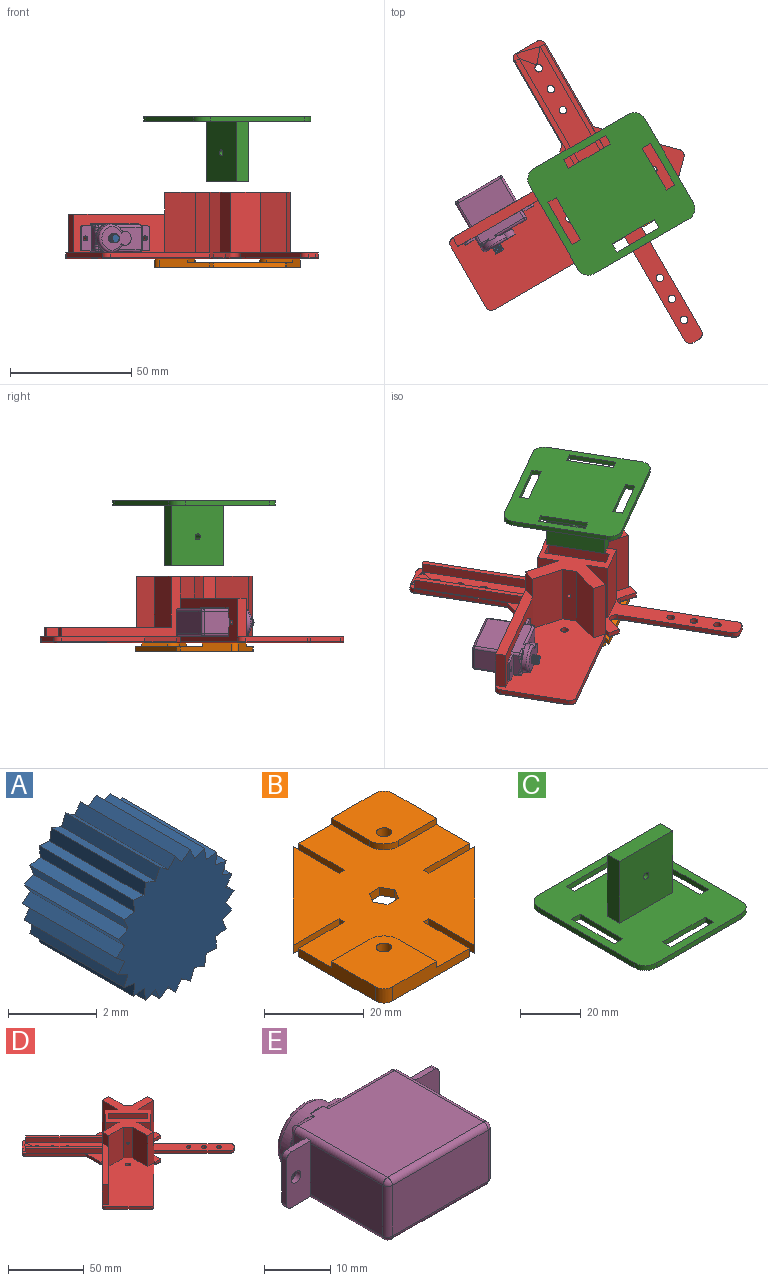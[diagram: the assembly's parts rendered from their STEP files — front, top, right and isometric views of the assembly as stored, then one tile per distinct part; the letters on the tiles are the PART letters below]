
ASSEMBLY  parts=5 mates=4
PART A: 50 faces, bbox 3.8x3x3.8 mm
  f0: plane 3x0.26mm, normal (0.78,0,-0.63), area 1mm2, adj f1,f47,f48,f49
  f1: plane 3x0.27mm, normal (-0.59,0,-0.81), area 1mm2, adj f0,f2,f48,f49
  f2: plane 3x0.31mm, normal (0.92,0,-0.4), area 1mm2, adj f1,f3,f48,f49
  f3: plane 3x0.32mm, normal (-0.36,0,-0.93), area 1mm2, adj f2,f4,f48,f49
  f4: plane 3x0.33mm, normal (0.99,0,-0.15), area 1mm2, adj f3,f5,f48,f49
  f5: plane 3x0.34mm, normal (-0.11,0,-0.99), area 1mm2, adj f4,f6,f48,f49
  f6: plane 3x0.34mm, normal (0.99,0,0.11), area 1mm2, adj f5,f7,f48,f49
  f7: plane 3x0.33mm, normal (0.15,0,-0.99), area 1mm2, adj f6,f8,f48,f49
  f8: plane 3x0.32mm, normal (0.93,0,0.36), area 1mm2, adj f7,f9,f48,f49
  f9: plane 3x0.31mm, normal (0.4,0,-0.92), area 1mm2, adj f8,f10,f48,f49
  f10: plane 3x0.27mm, normal (0.81,0,0.59), area 1mm2, adj f9,f11,f48,f49
  f11: plane 3x0.26mm, normal (0.63,0,-0.78), area 1mm2, adj f10,f12,f48,f49
  f12: plane 3x0.26mm, normal (0.63,0,0.78), area 1mm2, adj f11,f13,f48,f49
  f13: plane 3x0.27mm, normal (0.81,0,-0.59), area 1mm2, adj f12,f14,f48,f49
  f14: plane 3x0.31mm, normal (0.4,0,0.92), area 1mm2, adj f13,f15,f48,f49
  f15: plane 3x0.32mm, normal (0.93,0,-0.36), area 1mm2, adj f14,f16,f48,f49
  f16: plane 3x0.33mm, normal (0.15,0,0.99), area 1mm2, adj f15,f17,f48,f49
  f17: plane 3x0.34mm, normal (0.99,0,-0.11), area 1mm2, adj f16,f18,f48,f49
  f18: plane 3x0.34mm, normal (-0.11,0,0.99), area 1mm2, adj f17,f19,f48,f49
  f19: plane 3x0.33mm, normal (0.99,0,0.15), area 1mm2, adj f18,f20,f48,f49
  f20: plane 3x0.32mm, normal (-0.36,0,0.93), area 1mm2, adj f19,f21,f48,f49
  f21: plane 3x0.31mm, normal (0.92,0,0.4), area 1mm2, adj f20,f22,f48,f49
  f22: plane 3x0.27mm, normal (-0.59,0,0.81), area 1mm2, adj f21,f23,f48,f49
  f23: plane 3x0.26mm, normal (0.78,0,0.63), area 1mm2, adj f22,f24,f48,f49
  f24: plane 3x0.26mm, normal (-0.78,0,0.63), area 1mm2, adj f23,f25,f48,f49
  f25: plane 3x0.27mm, normal (0.59,0,0.81), area 1mm2, adj f24,f26,f48,f49
  f26: plane 3x0.31mm, normal (-0.92,0,0.4), area 1mm2, adj f25,f27,f48,f49
  f27: plane 3x0.32mm, normal (0.36,0,0.93), area 1mm2, adj f26,f28,f48,f49
  f28: plane 3x0.33mm, normal (-0.99,0,0.15), area 1mm2, adj f27,f29,f48,f49
  f29: plane 3x0.34mm, normal (0.11,0,0.99), area 1mm2, adj f28,f30,f48,f49
  f30: plane 3x0.34mm, normal (-0.99,0,-0.11), area 1mm2, adj f29,f31,f48,f49
  f31: plane 3x0.33mm, normal (-0.15,0,0.99), area 1mm2, adj f30,f32,f48,f49
  f32: plane 3x0.32mm, normal (-0.93,0,-0.36), area 1mm2, adj f31,f33,f48,f49
  f33: plane 3x0.31mm, normal (-0.4,0,0.92), area 1mm2, adj f32,f34,f48,f49
  f34: plane 3x0.27mm, normal (-0.81,0,-0.59), area 1mm2, adj f33,f35,f48,f49
  f35: plane 3x0.26mm, normal (-0.63,0,0.78), area 1mm2, adj f34,f36,f48,f49
  f36: plane 3x0.26mm, normal (-0.63,0,-0.78), area 1mm2, adj f35,f37,f48,f49
  f37: plane 3x0.27mm, normal (-0.81,0,0.59), area 1mm2, adj f36,f38,f48,f49
  f38: plane 3x0.31mm, normal (-0.4,0,-0.92), area 1mm2, adj f37,f39,f48,f49
  f39: plane 3x0.32mm, normal (-0.93,0,0.36), area 1mm2, adj f38,f40,f48,f49
  f40: plane 3x0.33mm, normal (-0.15,0,-0.99), area 1mm2, adj f39,f41,f48,f49
  f41: plane 3x0.34mm, normal (-0.99,0,0.11), area 1mm2, adj f40,f42,f48,f49
  f42: plane 3x0.34mm, normal (0.11,0,-0.99), area 1mm2, adj f41,f43,f48,f49
  f43: plane 3x0.33mm, normal (-0.99,0,-0.15), area 1mm2, adj f42,f44,f48,f49
  f44: plane 3x0.32mm, normal (0.36,0,-0.93), area 1mm2, adj f43,f45,f48,f49
  f45: plane 3x0.31mm, normal (-0.92,0,-0.4), area 1mm2, adj f44,f46,f48,f49
  f46: plane 3x0.27mm, normal (0.59,0,-0.81), area 1mm2, adj f45,f47,f48,f49
  f47: plane 3x0.26mm, normal (-0.78,0,-0.63), area 1mm2, adj f0,f46,f48,f49
  f48: plane 3.75x3.75mm, normal (0,-1,0), area 9.5mm2, adj f0,f1,f2,f3,f4,f5,f6,f7
  f49: plane 3.75x3.75mm, normal (0,1,0), area 9.5mm2, adj f0,f1,f2,f3,f4,f5,f6,f7
PART B: 38 faces, bbox 50x50x3.5 mm
  f0: plane 50x50mm, normal (0,0,1), area 1374.3mm2, adj f1,f2,f3,f4,f5,f6,f7,f8
  f1: plane 13x2mm, normal (-1,0,0), area 26mm2, adj f0,f2,f28,f29
  f2: plane 2x1.5mm, normal (0,1,0), area 3mm2, adj f0,f1,f3,f29
  f3: plane 13x2mm, normal (1,0,0), area 26mm2, adj f0,f2,f4,f29
  f4: plane 24.25x24.25mm, normal (-0.71,0.71,0), area 68.6mm2, adj f0,f3,f5,f29
  f5: plane 13x2mm, normal (0,-1,0), area 26mm2, adj f0,f4,f6,f29
  f6: plane 2x1.5mm, normal (-1,0,0), area 3mm2, adj f0,f5,f7,f29
  f7: plane 13x2mm, normal (0,1,0), area 26mm2, adj f0,f6,f8,f29
  f8: plane 21.75x3.5mm, normal (-1,0,0), area 62mm2, adj f0,f7,f9,f29,f34,f37
  f9: cylinder r=2.5mm len=3.5mm, axis (0,0,-1), area 13.7mm2, adj f8,f10,f29,f37
  f10: plane 21.75x3.5mm, normal (0,-1,0), area 62mm2, adj f0,f9,f11,f29,f35,f37
  f11: plane 13x2mm, normal (1,0,0), area 26mm2, adj f0,f10,f12,f29
  f12: plane 2x1.5mm, normal (0,-1,0), area 3mm2, adj f0,f11,f13,f29
  f13: plane 13x2mm, normal (-1,0,0), area 26mm2, adj f0,f12,f14,f29
  f14: plane 24.25x24.25mm, normal (0.71,-0.71,0), area 68.6mm2, adj f0,f13,f15,f29
  f15: plane 13x2mm, normal (0,1,0), area 26mm2, adj f0,f14,f16,f29
  f16: plane 2x1.5mm, normal (1,0,0), area 3mm2, adj f0,f15,f17,f29
  f17: plane 13x2mm, normal (0,-1,0), area 26mm2, adj f0,f16,f18,f29
  f18: plane 21.75x3.5mm, normal (1,0,0), area 62mm2, adj f0,f17,f19,f29,f32,f33
  f19: cylinder r=2.5mm len=3.5mm, axis (0,0,-1), area 13.7mm2, adj f18,f28,f29,f33
  f20: plane 2.68x2mm, normal (-0.87,0.5,0), area 6.2mm2, adj f0,f21,f25,f29
  f21: plane 3.1x2mm, normal (0,1,0), area 6.2mm2, adj f0,f20,f22,f29
  f22: plane 2.68x2mm, normal (0.87,0.5,0), area 6.2mm2, adj f0,f21,f23,f29
  f23: plane 2.68x2mm, normal (0.87,-0.5,0), area 6.2mm2, adj f0,f22,f24,f29
  f24: plane 3.1x2mm, normal (0,-1,0), area 6.2mm2, adj f0,f23,f25,f29
  f25: plane 2.68x2mm, normal (-0.87,-0.5,0), area 6.2mm2, adj f0,f20,f24,f29
  f26: cylinder r=1.55mm len=3.5mm, axis (0,0,-1), area 34.1mm2, adj f29,f33
  f27: cylinder r=1.55mm len=3.5mm, axis (0,0,-1), area 34.1mm2, adj f29,f37
  f28: plane 21.75x3.5mm, normal (0,1,0), area 62mm2, adj f0,f1,f19,f29,f30,f33
  f29: plane 50x50mm, normal (0,0,-1), area 1791.2mm2, adj f1,f2,f3,f4,f5,f6,f7,f8
  f30: plane 10.86x1.5mm, normal (-1,0,0), area 16.3mm2, adj f0,f28,f31,f33
  f31: cylinder r=4mm len=4mm, axis (0,0,-1), area 9.4mm2, adj f0,f30,f32,f33
  f32: plane 10.86x1.5mm, normal (0,-1,0), area 16.3mm2, adj f0,f18,f31,f33
  f33: plane 14.86x14.86mm, normal (0,0,1), area 208.4mm2, adj f18,f19,f26,f28,f30,f31,f32
  f34: plane 10.86x1.5mm, normal (0,1,0), area 16.3mm2, adj f0,f8,f36,f37
  f35: plane 10.86x1.5mm, normal (1,0,0), area 16.3mm2, adj f0,f10,f36,f37
  f36: cylinder r=4mm len=4mm, axis (0,0,-1), area 9.4mm2, adj f0,f34,f35,f37
  f37: plane 14.86x14.86mm, normal (0,0,1), area 208.4mm2, adj f8,f9,f10,f27,f34,f35,f36
PART C: 32 faces, bbox 50x55x27 mm
  f0: plane 55x50mm, normal (0,0,1), area 2263.5mm2, adj f1,f2,f3,f4,f5,f6,f7,f8
  f1: plane 4x2mm, normal (1,0,0), area 8mm2, adj f0,f2,f24,f25
  f2: plane 20x2mm, normal (0,-1,0), area 40mm2, adj f0,f1,f3,f25
  f3: plane 4x2mm, normal (-1,0,0), area 8mm2, adj f0,f2,f24,f25
  f4: plane 45x2mm, normal (1,0,0), area 90mm2, adj f0,f5,f20,f25
  f5: cylinder r=5mm len=5mm, axis (0,0,-1), area 15.7mm2, adj f0,f4,f6,f25
  f6: plane 40x2mm, normal (0,1,0), area 80mm2, adj f0,f5,f7,f25
  f7: cylinder r=5mm len=5mm, axis (0,0,-1), area 15.7mm2, adj f0,f6,f8,f25
  f8: plane 45x2mm, normal (-1,0,0), area 90mm2, adj f0,f7,f9,f25
  f9: cylinder r=5mm len=5mm, axis (0,0,-1), area 15.7mm2, adj f0,f8,f10,f25
  f10: plane 40x2mm, normal (0,-1,0), area 80mm2, adj f0,f9,f20,f25
  f11: plane 4x2mm, normal (0,-1,0), area 8mm2, adj f0,f12,f21,f25
  f12: plane 20x2mm, normal (-1,0,0), area 40mm2, adj f0,f11,f13,f25
  f13: plane 4x2mm, normal (0,1,0), area 8mm2, adj f0,f12,f21,f25
  f14: plane 20x2mm, normal (1,0,0), area 40mm2, adj f0,f15,f22,f25
  f15: plane 4x2mm, normal (0,-1,0), area 8mm2, adj f0,f14,f16,f25
  f16: plane 20x2mm, normal (-1,0,0), area 40mm2, adj f0,f15,f22,f25
  f17: plane 4x2mm, normal (1,0,0), area 8mm2, adj f0,f18,f23,f25
  f18: plane 20x2mm, normal (0,-1,0), area 40mm2, adj f0,f17,f19,f25
  f19: plane 4x2mm, normal (-1,0,0), area 8mm2, adj f0,f18,f23,f25
  f20: cylinder r=5mm len=5mm, axis (0,0,-1), area 15.7mm2, adj f0,f4,f10,f25
  f21: plane 20x2mm, normal (1,0,0), area 40mm2, adj f0,f11,f13,f25
  f22: plane 4x2mm, normal (0,1,0), area 8mm2, adj f0,f14,f16,f25
  f23: plane 20x2mm, normal (0,1,0), area 40mm2, adj f0,f17,f19,f25
  f24: plane 20x2mm, normal (0,1,0), area 40mm2, adj f0,f1,f3,f25
  f25: plane 55x50mm, normal (0,0,-1), area 2408.5mm2, adj f1,f2,f3,f4,f5,f6,f7,f8
  f26: plane 25x25mm, normal (0,1,0), area 620.1mm2, adj f0,f27,f29,f30,f31
  f27: plane 25x5.8mm, normal (-1,0,0), area 145mm2, adj f0,f26,f28,f30
  f28: plane 25x25mm, normal (0,-1,0), area 620.1mm2, adj f0,f27,f29,f30,f31
  f29: plane 25x5.8mm, normal (1,0,0), area 145mm2, adj f0,f26,f28,f30
  f30: plane 25x5.8mm, normal (0,0,1), area 145mm2, adj f26,f27,f28,f29
  f31: cylinder r=1.25mm len=5.8mm, axis (0,-1,0), area 45.6mm2, adj f26,f28
PART D: 144 faces, bbox 111x113.5x27.5 mm
  f0: plane 25x9.9mm, normal (-0.71,0.71,0), area 334mm2, adj f1,f66,f67,f75,f138,f140,f142,f143
  f1: plane 53.02x53.02mm, normal (0,0,1), area 782.5mm2, adj f0,f11,f12,f13,f14,f15,f16,f17
  f2: plane 58.57x52.57mm, normal (0,0,1), area 1637.9mm2, adj f22,f23,f24,f25,f26,f48,f68,f69
  f3: plane 9x6mm, normal (-1,0,0), area 54mm2, adj f21,f68,f75,f86
  f4: plane 50.54x50.54mm, normal (0,0,1), area 540.4mm2, adj f29,f30,f31,f32,f33,f34,f35,f36
  f5: plane 18.25x18.25mm, normal (0,0,1), area 315.2mm2, adj f6,f7,f8,f49,f63,f64,f65
  f6: plane 27x21.75mm, normal (1,0,0), area 193.5mm2, adj f5,f7,f52,f63,f75,f133
  f7: cylinder r=2.5mm len=2.5mm, axis (0,0,-1), area 7.9mm2, adj f5,f6,f8,f131
  f8: plane 27x21.75mm, normal (0,1,0), area 193.5mm2, adj f5,f7,f9,f65,f75,f129
  f9: plane 27x17.5mm, normal (-1,0,0), area 431.3mm2, adj f8,f10,f55,f66,f75,f127
  f10: plane 2x1.5mm, normal (0,1,0), area 3mm2, adj f9,f11,f55,f125
  f11: plane 17.5x2mm, normal (1,0,0), area 35mm2, adj f1,f10,f12,f55,f123
  f12: plane 13.64x2mm, normal (0,1,0), area 27.3mm2, adj f1,f11,f13,f121
  f13: plane 28.03x28.03mm, normal (0.71,0.71,0), area 79.3mm2, adj f1,f12,f14,f119
  f14: cylinder r=2.5mm len=3.54mm, axis (0,0,-1), area 7.9mm2, adj f1,f13,f15,f117
  f15: plane 7.07x7.07mm, normal (-0.71,0.71,0), area 20mm2, adj f1,f14,f16,f115
  f16: cylinder r=2.5mm len=3.54mm, axis (0,0,-1), area 7.9mm2, adj f1,f15,f17,f113
  f17: plane 28.03x28.03mm, normal (-0.71,-0.71,0), area 79.3mm2, adj f1,f16,f18,f111
  f18: plane 13.64x2mm, normal (-1,0,0), area 27.3mm2, adj f1,f17,f19,f109
  f19: plane 17.5x2mm, normal (0,-1,0), area 35mm2, adj f1,f18,f20,f56,f107
  f20: plane 2x1.5mm, normal (-1,0,0), area 3mm2, adj f19,f21,f56,f105
  f21: plane 27x17.5mm, normal (0,1,0), area 431.3mm2, adj f3,f20,f22,f56,f67,f75,f103
  f22: plane 33.59x33.59mm, normal (-0.71,0.71,0), area 573.5mm2, adj f2,f21,f23,f77,f78,f79,f80,f81
  f23: cylinder r=2.5mm len=3.54mm, axis (0,0,-1), area 7.9mm2, adj f2,f22,f24,f99
  f24: plane 20.71x20.71mm, normal (-0.71,-0.71,0), area 58.6mm2, adj f2,f23,f25,f100
  f25: cylinder r=2.5mm len=3.54mm, axis (0,0,-1), area 7.9mm2, adj f2,f24,f26,f102
  f26: plane 33.59x33.59mm, normal (0.71,-0.71,0), area 95mm2, adj f2,f25,f27,f104
  f27: plane 27x17.5mm, normal (1,0,0), area 431.3mm2, adj f26,f28,f57,f71,f72,f75,f106
  f28: plane 2x1.5mm, normal (0,-1,0), area 3mm2, adj f27,f29,f57,f108
  f29: plane 17.5x2mm, normal (-1,0,0), area 35mm2, adj f4,f28,f30,f57,f110
  f30: plane 5x2mm, normal (0,-1,0), area 10mm2, adj f4,f29,f31,f112
  f31: plane 7.56x2mm, normal (1,0,0), area 15.1mm2, adj f4,f30,f32,f114
  f32: cylinder r=2.5mm len=4.27mm, axis (0,0,-1), area 11.8mm2, adj f4,f31,f33,f116
  f33: plane 34.88x34.88mm, normal (-0.71,-0.71,0), area 98.7mm2, adj f4,f32,f34,f118
  f34: cylinder r=2.5mm len=3.54mm, axis (0,0,-1), area 7.9mm2, adj f4,f33,f35,f120
  f35: plane 2.12x2.12mm, normal (0.71,-0.71,0), area 6mm2, adj f4,f34,f36,f122
  f36: cylinder r=2.5mm len=3.54mm, axis (0,0,-1), area 7.9mm2, adj f4,f35,f37,f124
  f37: plane 34.88x34.88mm, normal (0.71,0.71,0), area 98.7mm2, adj f4,f36,f38,f126
  f38: cylinder r=2.5mm len=4.27mm, axis (0,0,-1), area 11.8mm2, adj f4,f37,f39,f128
  f39: plane 7.56x2mm, normal (0,-1,0), area 15.1mm2, adj f4,f38,f40,f130
  f40: plane 5x2mm, normal (1,0,0), area 10mm2, adj f4,f39,f41,f132
  f41: plane 17.5x2mm, normal (0,1,0), area 35mm2, adj f4,f40,f42,f58,f134
  f42: plane 2x1.5mm, normal (1,0,0), area 3mm2, adj f41,f52,f58,f136
  f43: cylinder r=1.55mm len=3.1mm, axis (0,0,-1), area 5.8mm2, adj f98,f137
  f44: cylinder r=1.55mm len=3.1mm, axis (0,0,-1), area 19.5mm2, adj f1,f97
  f45: cylinder r=1.55mm len=3.1mm, axis (0,0,-1), area 19.5mm2, adj f1,f96
  f46: cylinder r=1.55mm len=3.1mm, axis (0,0,-1), area 19.5mm2, adj f1,f95
  f47: cylinder r=1.55mm len=3.1mm, axis (0,0,-1), area 19.5mm2, adj f4,f94
  f48: cylinder r=1.55mm len=3.1mm, axis (0,0,-1), area 19.5mm2, adj f2,f93
  f49: cylinder r=1.55mm len=3.1mm, axis (0,0,-1), area 19.5mm2, adj f5,f92
  f50: cylinder r=1.55mm len=3.1mm, axis (0,0,-1), area 19.5mm2, adj f4,f91
  f51: cylinder r=1.55mm len=3.1mm, axis (0,0,-1), area 19.5mm2, adj f4,f90
  f52: plane 27x17.5mm, normal (0,-1,0), area 431.3mm2, adj f6,f42,f58,f62,f75,f135
  f53: plane 22.63x22.63mm, normal (0,0,1), area 128.7mm2, adj f59,f60,f61,f74,f137
  f54: plane 112.09x109.61mm, normal (0,0,-1), area 4089.8mm2, adj f90,f91,f92,f93,f94,f95,f96,f97
  f55: plane 3.15x1.5mm, normal (0,0,-1), area 3.6mm2, adj f9,f10,f11,f66
  f56: plane 3.15x1.5mm, normal (0,0,-1), area 3.6mm2, adj f19,f20,f21,f67
  f57: plane 3.15x1.5mm, normal (0,0,-1), area 3.6mm2, adj f27,f28,f29,f72
  f58: plane 3.15x1.5mm, normal (0,0,-1), area 3.6mm2, adj f41,f42,f52,f62
  f59: plane 25x18.38mm, normal (0.71,0.71,0), area 648.2mm2, adj f53,f60,f74,f75,f88
  f60: plane 25x4.24mm, normal (0.71,-0.71,0), area 150mm2, adj f53,f59,f61,f75
  f61: plane 25x18.38mm, normal (-0.71,-0.71,0), area 645.1mm2, adj f53,f60,f74,f75,f89
  f62: plane 25x6.41mm, normal (0.71,0.71,0), area 226.5mm2, adj f4,f52,f58,f73,f75
  f63: plane 25x14.01mm, normal (0,1,0), area 350.2mm2, adj f5,f6,f64,f75
  f64: plane 25x4.24mm, normal (0.71,0.71,0), area 145.1mm2, adj f5,f63,f65,f75,f89
  f65: plane 25x14.01mm, normal (1,0,0), area 350.2mm2, adj f5,f8,f64,f75
  f66: plane 43.53x43.53mm, normal (0.71,0.71,0), area 436.5mm2, adj f0,f1,f9,f55,f75,f141,f143
  f67: plane 43.53x43.53mm, normal (-0.71,-0.71,0), area 436.5mm2, adj f0,f1,f21,f56,f75,f139,f140
  f68: plane 25x14.01mm, normal (0,-1,0), area 350.2mm2, adj f2,f3,f69,f75,f76
  f69: plane 25x4.24mm, normal (-0.71,-0.71,0), area 148.2mm2, adj f2,f68,f70,f75,f88
  f70: plane 25x14.01mm, normal (-1,0,0), area 350.2mm2, adj f2,f69,f71,f75
  f71: plane 25x6mm, normal (0,-1,0), area 150mm2, adj f2,f27,f70,f75
  f72: plane 25x6.41mm, normal (-0.71,-0.71,0), area 226.5mm2, adj f4,f27,f57,f73,f75
  f73: plane 25x9.9mm, normal (0.71,-0.71,0), area 350mm2, adj f4,f62,f72,f75
  f74: plane 25x4.24mm, normal (-0.71,0.71,0), area 150mm2, adj f53,f59,f61,f75
  f75: plane 50x50mm, normal (0,0,1), area 721.4mm2, adj f0,f3,f6,f8,f9,f21,f27,f52
  f76: plane 30.59x30.59mm, normal (0.71,-0.71,0), area 410.6mm2, adj f2,f68,f77,f78,f79,f80,f81,f82
  f77: plane 12.1x3mm, normal (-0.71,-0.71,0), area 51.3mm2, adj f2,f22,f76,f78
  f78: plane 18.98x18.98mm, normal (0,0,-1), area 95.9mm2, adj f22,f76,f77,f79
  f79: plane 3.55x3mm, normal (0.71,0.71,0), area 15.1mm2, adj f22,f76,f78,f80
  f80: plane 3.71x3.71mm, normal (0.5,0.5,-0.71), area 6mm2, adj f22,f76,f79,f81
  f81: plane 3x3mm, normal (0.71,0.71,0), area 12.7mm2, adj f22,f76,f80,f82
  f82: plane 3.71x3.71mm, normal (0.5,0.5,0.71), area 6mm2, adj f22,f76,f81,f83
  f83: plane 3.55x3mm, normal (0.71,0.71,0), area 15.1mm2, adj f2,f22,f76,f82
  f84: plane 16x3mm, normal (-0.71,-0.71,0), area 67.9mm2, adj f2,f22,f76,f86
  f85: cylinder r=0.8mm len=4.13mm, axis (-0.71,0.71,0), area 21.3mm2, adj f22,f76
  f86: plane 36.59x33.59mm, normal (0,0,1), area 192.5mm2, adj f3,f22,f76,f84
  f87: cylinder r=0.8mm len=4.13mm, axis (-0.71,0.71,0), area 21.3mm2, adj f22,f76
  f88: cylinder r=0.75mm len=7.81mm, axis (-0.71,-0.71,0), area 45mm2, adj f59,f69
  f89: cylinder r=1.25mm len=8.52mm, axis (0.71,0.71,0), area 75mm2, adj f61,f64
  f90: torus R=2.05mm, axis (0,0,1), area 8.5mm2, adj f51,f54
  f91: torus R=2.05mm, axis (0,0,1), area 8.5mm2, adj f50,f54
  f92: torus R=2.05mm, axis (0,0,1), area 8.5mm2, adj f49,f54
  f93: torus R=2.05mm, axis (0,0,1), area 8.5mm2, adj f48,f54
  f94: torus R=2.05mm, axis (0,0,1), area 8.5mm2, adj f47,f54
  f95: torus R=2.05mm, axis (0,0,1), area 8.5mm2, adj f46,f54
  f96: torus R=2.05mm, axis (0,0,1), area 8.5mm2, adj f45,f54
  f97: torus R=2.05mm, axis (0,0,1), area 8.5mm2, adj f44,f54
  f98: torus R=2.05mm, axis (0,0,1), area 8.5mm2, adj f43,f54
  f99: torus R=2mm, axis (0,0,1), area 2.9mm2, adj f23,f54,f100,f101
  f100: cylinder r=0.5mm len=21.07mm, axis (0.71,-0.71,0), area 23mm2, adj f24,f54,f99,f102
  f101: cylinder r=0.5mm len=33.94mm, axis (-0.71,-0.71,0), area 37.2mm2, adj f22,f54,f99,f103
  f102: torus R=2mm, axis (0,0,1), area 2.9mm2, adj f25,f54,f100,f104
  f103: cylinder r=0.5mm len=18mm, axis (-1,0,0), area 13.8mm2, adj f21,f54,f101,f105
  f104: cylinder r=0.5mm len=33.94mm, axis (0.71,0.71,0), area 37.2mm2, adj f26,f54,f102,f106
  f105: cylinder r=0.5mm len=2.5mm, axis (0,-1,0), area 1.5mm2, adj f20,f54,f103,f107
  f106: cylinder r=0.5mm len=18mm, axis (0,1,0), area 13.8mm2, adj f27,f54,f104,f108
  f107: cylinder r=0.5mm len=18mm, axis (1,0,0), area 13.7mm2, adj f19,f54,f105,f109
  f108: cylinder r=0.5mm len=2.5mm, axis (1,0,0), area 1.5mm2, adj f28,f54,f106,f110
  f109: cylinder r=0.5mm len=13.85mm, axis (0,-1,0), area 10.6mm2, adj f18,f54,f107,f111
  f110: cylinder r=0.5mm len=18mm, axis (0,-1,0), area 13.7mm2, adj f29,f54,f108,f112
  f111: cylinder r=0.5mm len=28.53mm, axis (0.71,-0.71,0), area 31.2mm2, adj f17,f54,f109,f113
  f112: cylinder r=0.5mm len=5mm, axis (1,0,0), area 3.6mm2, adj f30,f54,f110,f114
  f113: torus R=2mm, axis (0,0,1), area 2.9mm2, adj f16,f54,f111,f115
  f114: cylinder r=0.5mm len=7.56mm, axis (0,1,0), area 5.8mm2, adj f31,f54,f112,f116
  f115: cylinder r=0.5mm len=7.42mm, axis (-0.71,-0.71,0), area 7.9mm2, adj f15,f54,f113,f117
  f116: torus R=3mm, axis (0,0,1), area 5mm2, adj f32,f54,f114,f118
  f117: torus R=2mm, axis (0,0,1), area 2.9mm2, adj f14,f54,f115,f119
  f118: cylinder r=0.5mm len=35.24mm, axis (0.71,-0.71,0), area 38.7mm2, adj f33,f54,f116,f120
  f119: cylinder r=0.5mm len=28.53mm, axis (-0.71,0.71,0), area 31.2mm2, adj f13,f54,f117,f121
  f120: torus R=2mm, axis (0,0,1), area 2.9mm2, adj f34,f54,f118,f122
  f121: cylinder r=0.5mm len=13.85mm, axis (-1,0,0), area 10.6mm2, adj f12,f54,f119,f123
  f122: cylinder r=0.5mm len=2.48mm, axis (0.71,0.71,0), area 2.4mm2, adj f35,f54,f120,f124
  f123: cylinder r=0.5mm len=18mm, axis (0,1,0), area 13.7mm2, adj f11,f54,f121,f125
  f124: torus R=2mm, axis (0,0,1), area 2.9mm2, adj f36,f54,f122,f126
  f125: cylinder r=0.5mm len=2.5mm, axis (-1,0,0), area 1.5mm2, adj f10,f54,f123,f127
  f126: cylinder r=0.5mm len=35.24mm, axis (-0.71,0.71,0), area 38.7mm2, adj f37,f54,f124,f128
  f127: cylinder r=0.5mm len=18mm, axis (0,-1,0), area 13.7mm2, adj f9,f54,f125,f129
  f128: torus R=3mm, axis (0,0,1), area 5mm2, adj f38,f54,f126,f130
  f129: cylinder r=0.5mm len=21.75mm, axis (-1,0,0), area 16.9mm2, adj f8,f54,f127,f131
  f130: cylinder r=0.5mm len=7.56mm, axis (1,0,0), area 5.8mm2, adj f39,f54,f128,f132
  f131: torus R=2mm, axis (0,0,1), area 2.9mm2, adj f7,f54,f129,f133
  f132: cylinder r=0.5mm len=5mm, axis (0,1,0), area 3.6mm2, adj f40,f54,f130,f134
  f133: cylinder r=0.5mm len=21.75mm, axis (0,1,0), area 16.9mm2, adj f6,f54,f131,f135
  f134: cylinder r=0.5mm len=18mm, axis (-1,0,0), area 13.7mm2, adj f41,f54,f132,f136
  f135: cylinder r=0.5mm len=18mm, axis (1,0,0), area 13.7mm2, adj f52,f54,f133,f136
  f136: cylinder r=0.5mm len=2.5mm, axis (0,1,0), area 1.5mm2, adj f42,f54,f134,f135
  f137: cone r=1.55mm half-angle=45deg, axis (0,0,1), area 28mm2, adj f43,f53
  f138: plane 37.12x37.12mm, normal (0.71,0.71,0), area 210mm2, adj f0,f1,f139,f140
  f139: plane 4x1.41mm, normal (-0.71,0.71,0), area 8mm2, adj f1,f67,f138,f140
  f140: plane 38.54x38.54mm, normal (0,0,1), area 105mm2, adj f0,f67,f138,f139
  f141: plane 4x1.41mm, normal (-0.71,0.71,0), area 8mm2, adj f1,f66,f142,f143
  f142: plane 37.12x37.12mm, normal (-0.71,-0.71,0), area 210mm2, adj f0,f1,f141,f143
  f143: plane 38.54x38.54mm, normal (0,0,1), area 105mm2, adj f0,f66,f141,f142
PART E: 70 faces, bbox 32.5x24x12.7 mm
  f0: torus R=3.12mm, axis (0,1,0), area 4.4mm2, adj f5,f13,f67,f68
  f1: torus R=4.87mm, axis (0,1,0), area 46.2mm2, adj f4,f5,f10
  f2: cylinder r=1.03mm len=2.06mm, axis (0,1,0), area 6.5mm2, adj f28,f29
  f3: cylinder r=1.03mm len=2.06mm, axis (0,1,0), area 6.5mm2, adj f22,f23
  f4: cylinder r=5.87mm len=11.74mm, axis (0,1,0), area 60.7mm2, adj f1,f5,f8,f9,f15,f17,f58,f59
  f5: cylinder r=2.87mm len=5.74mm, axis (0,1,0), area 31.7mm2, adj f0,f1,f4,f10
  f6: plane 15.51x9.38mm, normal (1,0,0), area 145.5mm2, adj f23,f35,f36,f42
  f7: plane 9.38x3.49mm, normal (-1,0,0), area 25.8mm2, adj f28,f33,f34,f45,f46,f51,f52
  f8: plane 2.87x0.18mm, normal (0,-1,0), area 0.3mm2, adj f4,f17
  f9: plane 2.87x0.18mm, normal (0,-1,0), area 0.3mm2, adj f4,f15
  f10: plane 14.01x9.74mm, normal (0,1,0), area 96mm2, adj f1,f5
  f11: plane 0.98x0.94mm, normal (0,1,0), area 0.4mm2, adj f46,f48,f60
  f12: plane 0.98x0.94mm, normal (0,1,0), area 0.4mm2, adj f49,f52,f64
  f13: plane 11.63x9.38mm, normal (0,1,0), area 76.9mm2, adj f0,f53,f55,f57,f67,f68
  f14: plane 15.51x9.38mm, normal (-1,0,0), area 145.5mm2, adj f29,f33,f34,f39
  f15: plane 20.43x20.01mm, normal (0,0,-1), area 391mm2, adj f4,f9,f33,f35,f38,f48,f57,f61
  f16: plane 9.38x2.49mm, normal (1,0,0), area 23.4mm2, adj f22,f35,f36,f55
  f17: plane 20.43x20.01mm, normal (0,0,1), area 391mm2, adj f4,f8,f34,f36,f43,f49,f53,f65
  f18: plane 20.43x9.38mm, normal (0,-1,0), area 191.6mm2, adj f38,f39,f42,f43
  f19: cylinder r=1mm len=1mm, axis (0,-1,0), area 1.6mm2, adj f20,f22,f23,f24
  f20: plane 8.29x1mm, normal (1,0,0), area 8.3mm2, adj f19,f21,f22,f23
  f21: cylinder r=1mm len=1mm, axis (0,-1,0), area 1.6mm2, adj f20,f22,f23,f25
  f22: plane 10.29x5.17mm, normal (0,1,0), area 48.3mm2, adj f3,f16,f19,f20,f21,f24,f25,f35
  f23: plane 10.29x5.17mm, normal (0,-1,0), area 48.3mm2, adj f3,f6,f19,f20,f21,f24,f25,f35
  f24: plane 4.17x1mm, normal (0,0,1), area 4.2mm2, adj f19,f22,f23,f36
  f25: plane 4.17x1mm, normal (0,0,-1), area 4.2mm2, adj f21,f22,f23,f35
  f26: plane 4.17x1mm, normal (0,0,-1), area 4.2mm2, adj f28,f29,f30,f33
  f27: plane 4.17x1mm, normal (0,0,1), area 4.2mm2, adj f28,f29,f32,f34
  f28: plane 10.29x5.17mm, normal (0,1,0), area 48.3mm2, adj f2,f7,f26,f27,f30,f31,f32,f33
  f29: plane 10.29x5.17mm, normal (0,-1,0), area 48.3mm2, adj f2,f14,f26,f27,f30,f31,f32,f33
  f30: cylinder r=1mm len=1mm, axis (0,-1,0), area 1.6mm2, adj f26,f28,f29,f31
  f31: plane 8.29x1mm, normal (-1,0,0), area 8.3mm2, adj f28,f29,f30,f32
  f32: cylinder r=1mm len=1mm, axis (0,-1,0), area 1.6mm2, adj f27,f28,f29,f31
  f33: cylinder r=1mm len=19mm, axis (0,1,0), area 29.4mm2, adj f7,f14,f15,f26,f28,f29,f37,f47
  f34: cylinder r=1mm len=19mm, axis (0,1,0), area 29.4mm2, adj f7,f14,f17,f27,f28,f29,f41,f50
  f35: cylinder r=1mm len=19mm, axis (0,1,0), area 29.4mm2, adj f6,f15,f16,f22,f23,f25,f40,f56
  f36: cylinder r=1mm len=19mm, axis (0,1,0), area 29.4mm2, adj f6,f16,f17,f22,f23,f24,f44,f54
  f37: sphere r=1mm, area 2.1mm2, adj f33,f38,f39
  f38: cylinder r=1mm len=20.43mm, axis (1,0,0), area 32.1mm2, adj f15,f18,f37,f40
  f39: cylinder r=1mm len=9.38mm, axis (0,0,-1), area 14.7mm2, adj f14,f18,f37,f41
  f40: sphere r=1mm, area 1mm2, adj f35,f38,f42
  f41: sphere r=1mm, area 1.6mm2, adj f34,f39,f43
  f42: cylinder r=1mm len=9.38mm, axis (0,0,1), area 14.7mm2, adj f6,f18,f40,f44
  f43: cylinder r=1mm len=20.43mm, axis (-1,0,0), area 32.1mm2, adj f17,f18,f41,f44
  f44: sphere r=1mm, area 1.6mm2, adj f36,f42,f43
  f45: bspline ~3.28x1mm, area 1.4mm2, adj f7,f46,f58
  f46: cylinder r=1mm len=1.41mm, axis (0,0,1), area 2.2mm2, adj f7,f11,f45,f47,f59
  f47: sphere r=1mm, area 2.1mm2, adj f33,f46,f48
  f48: cylinder r=1mm len=3.4mm, axis (-1,0,0), area 3.4mm2, adj f11,f15,f47,f61
  f49: cylinder r=1mm len=3.4mm, axis (1,0,0), area 3.4mm2, adj f12,f17,f50,f65
  f50: sphere r=1mm, area 1.6mm2, adj f34,f49,f52
  f51: bspline ~3.28x1mm, area 1.4mm2, adj f7,f52,f62
  f52: cylinder r=1mm len=1.41mm, axis (0,0,1), area 2.2mm2, adj f7,f12,f50,f51,f63
  f53: cylinder r=1mm len=14.1mm, axis (1,0,0), area 20.2mm2, adj f13,f17,f54,f66
  f54: sphere r=1mm, area 1.6mm2, adj f36,f53,f55
  f55: cylinder r=1mm len=9.38mm, axis (0,0,-1), area 14.7mm2, adj f13,f16,f54,f56
  f56: sphere r=1mm, area 1mm2, adj f35,f55,f57
  f57: cylinder r=1mm len=14.1mm, axis (-1,0,0), area 20.2mm2, adj f13,f15,f56,f69
  f58: bspline ~3.28x0.93mm, area 0.5mm2, adj f4,f45,f59
  f59: bspline ~0.56x0.44mm, area 0.2mm2, adj f4,f46,f58,f60
  f60: torus R=6.12mm, axis (0,1,0), area 0.5mm2, adj f4,f11,f59,f61
  f61: bspline ~2.53x1.27mm, area 0.7mm2, adj f4,f15,f48,f60
  f62: bspline ~3.28x0.93mm, area 0.5mm2, adj f4,f51,f63
  f63: bspline ~0.56x0.44mm, area 0.2mm2, adj f4,f52,f62,f64
  f64: torus R=6.12mm, axis (0,1,0), area 0.5mm2, adj f4,f12,f63,f65
  f65: bspline ~2.53x1.27mm, area 0.7mm2, adj f4,f17,f49,f64
  f66: bspline ~2.53x1.27mm, area 0.7mm2, adj f4,f17,f53,f67
  f67: torus R=6.12mm, axis (0,1,0), area 0.9mm2, adj f0,f4,f13,f66
  f68: torus R=6.12mm, axis (0,1,0), area 0.9mm2, adj f0,f4,f13,f69
  f69: bspline ~2.53x1.27mm, area 0.7mm2, adj f4,f15,f57,f68
PLACE A rot(axis=(-0.97,-0.26,0),180deg) t=(-44.81,-24.4,14.89)mm
PLACE B rot(axis=(0,0,-1),15deg) t=(1.28,-0.58,2.89)mm
PLACE C rot(axis=(-0.87,0.5,0),180deg) t=(25.09,13.17,65.19)mm
PLACE D rot(axis=(0,0,-1),15deg) t=(1.28,-0.58,6.39)mm
PLACE E rot(axis=(-0.97,-0.26,0),180deg) t=(-46.31,-21.8,14.89)mm
MATE fastened B.f26 <-> D.f49  axis (0,0,1) through (18.6,9.42,6.39)mm
MATE slider C.f30 <-> D.f43  axis (0,0,-1) through (1.28,-0.58,38.19)mm
MATE fastened D.f87 <-> E.f2  axis (0.5,-0.87,0) through (-57.75,-19.76,14.89)mm
MATE fastened A.f48 <-> E.f1  axis (-0.5,0.87,0) through (-46.31,-21.8,14.89)mm
